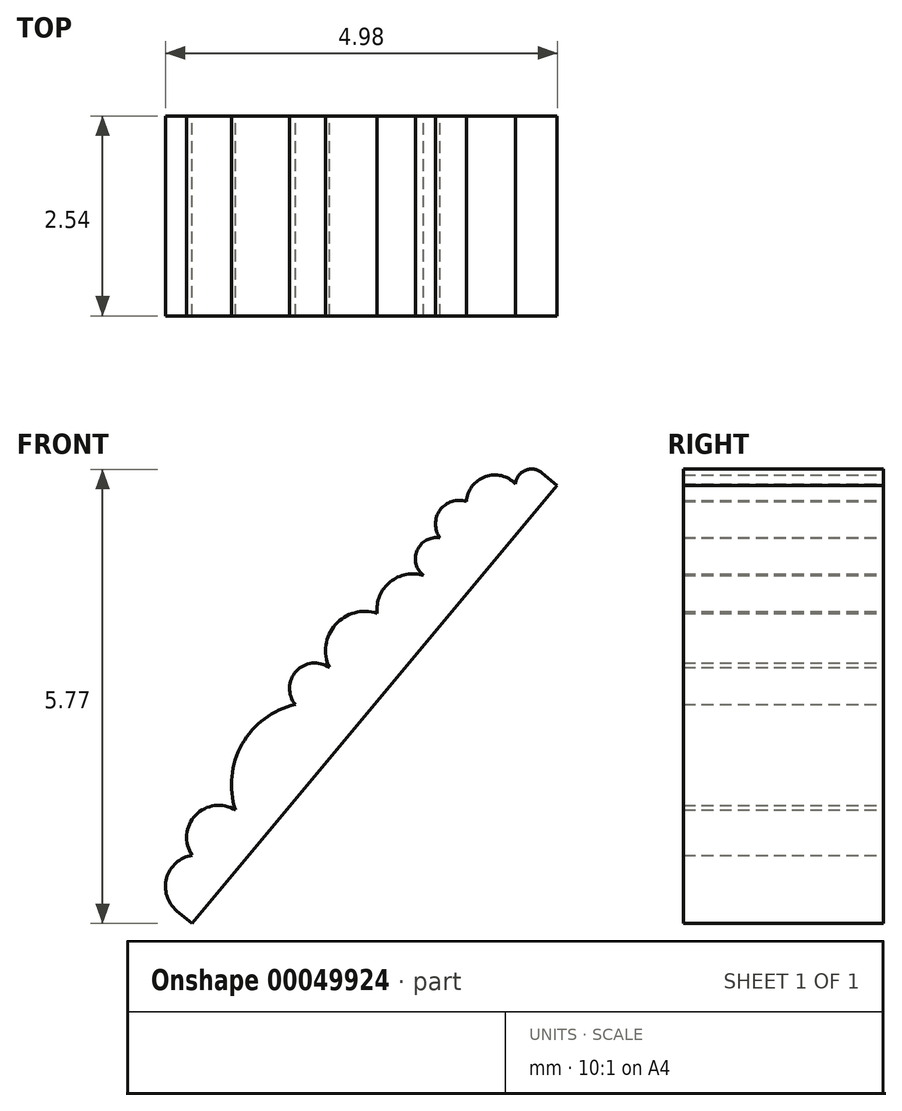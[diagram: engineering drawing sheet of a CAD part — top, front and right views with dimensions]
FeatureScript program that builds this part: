
annotation { "Feature Type Name" : "Feature", "Feature Type Description" : "" }
export const myFeature = defineFeature(function(context is Context, id is Id, definition is map)
    precondition{}
    {
        {
            var Q0;
            Q0=qCreatedBy(makeId("Front.planeOp"),FACE);
            var sketch = newSketch(context, id + "F0", { "sketchPlane" : qUnion([Q0])});
            skLineSegment(sketch, "E0", {"start": v(-15.05, 26.71) * mm, "end": v(-19.7, 21.15) * mm});
            skLineSegment(sketch, "E1", {"start": v(-19.7, 21.15) * mm, "end": v(-19.89, 21.31) * mm});
            skArc(sketch, "E2", {"start": v(-19.7, 22.02) * mm, "mid": v(-20.02, 21.73) * mm, "end": v(-19.89, 21.31) * mm});
            skArc(sketch, "E3", {"start": v(-19.14, 22.6) * mm, "mid": v(-19.65, 22.53) * mm, "end": v(-19.7, 22.02) * mm});
            skArc(sketch, "E4", {"start": v(-18.38, 23.93) * mm, "mid": v(-19.06, 23.43) * mm, "end": v(-19.14, 22.6) * mm});
            skPoint(sketch, "E4.startSnap0", {"position": v(-17.37, 23.93) * mm});
            skArc(sketch, "E5", {"start": v(-17.95, 24.4) * mm, "mid": v(-18.37, 24.36) * mm, "end": v(-18.38, 23.93) * mm});
            skArc(sketch, "E6", {"start": v(-17.34, 25.1) * mm, "mid": v(-17.87, 24.95) * mm, "end": v(-17.95, 24.4) * mm});
            skArc(sketch, "E7", {"start": v(-16.75, 25.57) * mm, "mid": v(-17.18, 25.5) * mm, "end": v(-17.34, 25.1) * mm});
            skArc(sketch, "E8", {"start": v(-16.54, 26.05) * mm, "mid": v(-16.83, 25.9) * mm, "end": v(-16.75, 25.57) * mm});
            skArc(sketch, "E9", {"start": v(-16.2, 26.51) * mm, "mid": v(-16.54, 26.4) * mm, "end": v(-16.54, 26.05) * mm});
            skArc(sketch, "E10", {"start": v(-15.58, 26.74) * mm, "mid": v(-15.97, 26.83) * mm, "end": v(-16.2, 26.51) * mm});
            skLineSegment(sketch, "E11", {"start": v(-15.05, 26.71) * mm, "end": v(-15.25, 26.88) * mm});
            skArc(sketch, "E12", {"start": v(-15.25, 26.88) * mm, "mid": v(-15.46, 26.9) * mm, "end": v(-15.58, 26.74) * mm});
            skSolve(sketch);
        }
        {
            var Q0;
            Q0 = qSketchRegion(id + "F0", true);
            extrude(context, id + "F1", {"entities" : qUnion([Q0]), "depth" : 2.54 * mm});
        }
    });
